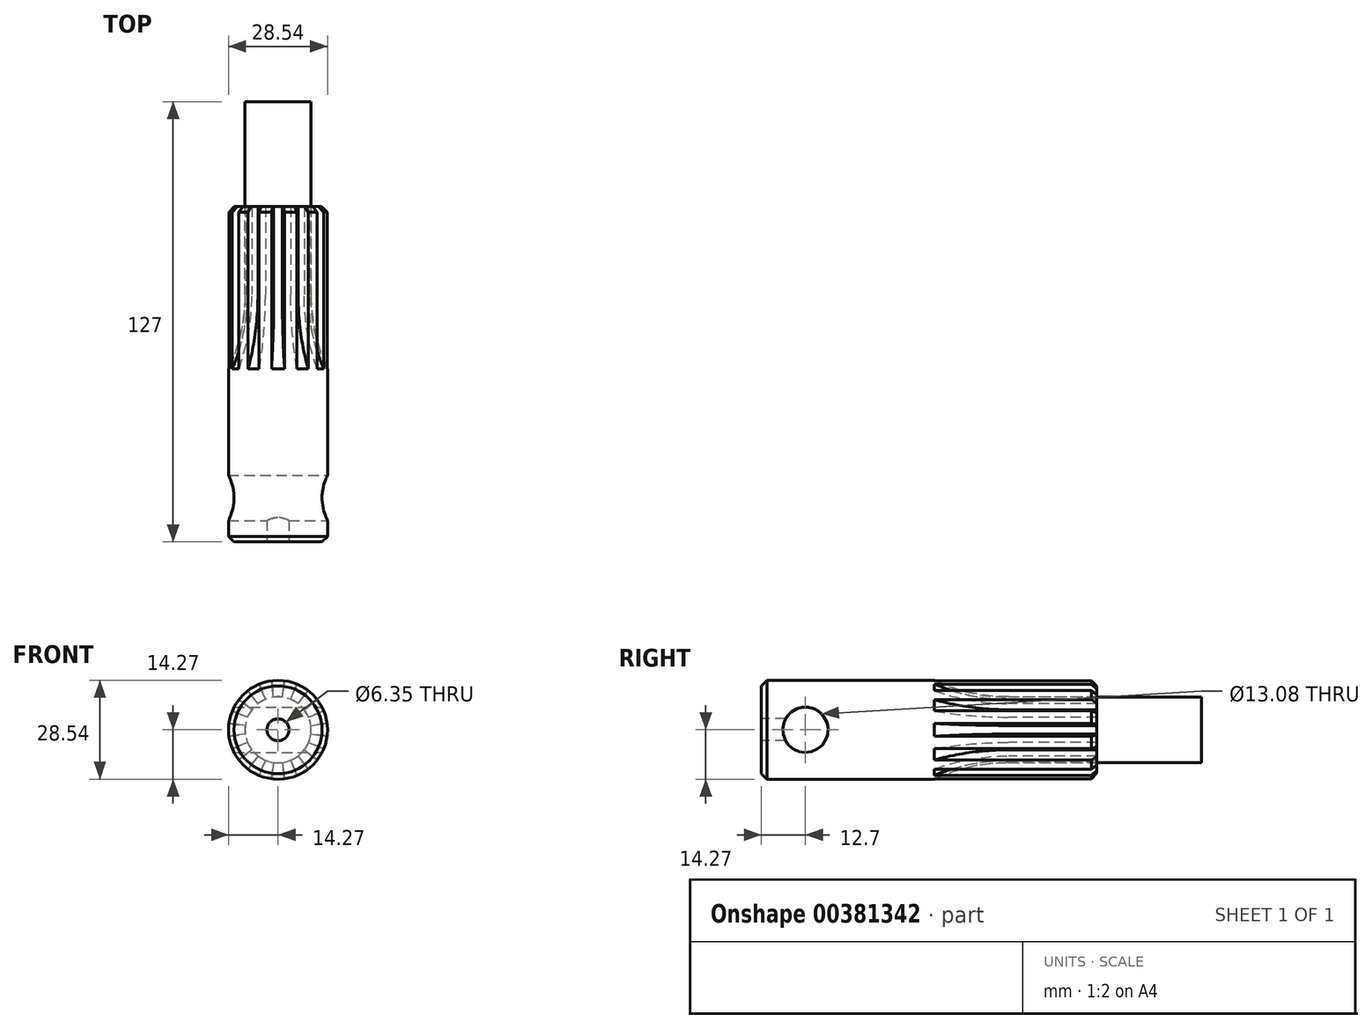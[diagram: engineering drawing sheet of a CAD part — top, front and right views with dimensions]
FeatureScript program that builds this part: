
annotation { "Feature Type Name" : "Feature", "Feature Type Description" : "" }
export const myFeature = defineFeature(function(context is Context, id is Id, definition is map)
    precondition{}
    {
        {
            var Q0;
            Q0=qCreatedBy(makeId("Right.planeOp"),FACE);
            var sketch = newSketch(context, id + "F0", { "sketchPlane" : qUnion([Q0])});
            skLineSegment(sketch, "E0", {"start": v(-154.35, 0) * mm, "end": v(99.65, 0) * mm});
            skSolve(sketch);
        }
        {
            var Q0;
            Q0=qCreatedBy(makeId("Front.planeOp"),FACE);
            var sketch = newSketch(context, id + "F1", { "sketchPlane" : qUnion([Q0])});
            skCircle(sketch, "E1", {"center": v(0, 0) * mm, "radius": 9.51 * mm});
            skSolve(sketch);
        }
        {
            var Q0;
            Q0=qSketchRegion(id+"F1",true);
            extrude(context, id + "F2", {"entities" : qUnion([Q0]), "depth" : 127 * mm});
        }
        {
            var Q0;
            Q0=makeQuery(id+"F2.opExtrude","CAP_FACE",FACE,{"disambiguationData":[OSD([sQuery(id+"F1.wireOp",EDGE,"E1")])],"isStart":false});
            var sketch = newSketch(context, id + "F3", { "sketchPlane" : qUnion([Q0])});
            skCircle(sketch, "E2", {"center": v(0, 0) * mm, "radius": 14.27 * mm});
            skSolve(sketch);
        }
        {
            var Q0;
            Q0=qSketchRegion(id+"F3",true);
            extrude(context, id + "F4", {"entities" : qUnion([Q0]), "operationType" : NewBodyOperationType.ADD, "oppositeDirection" : true, "depth" : 96.77 * mm});
        }
        {
            var Q0;
            Q0=qCreatedBy(makeId("Right.planeOp"),FACE);
            var sketch = newSketch(context, id + "F5", { "sketchPlane" : qUnion([Q0])});
            skCircle(sketch, "E3", {"center": v(-114.3, 0) * mm, "radius": 6.54 * mm});
            skSolve(sketch);
        }
        {
            var Q0;
            Q0=qSketchRegion(id+"F5",true);
            extrude(context, id + "F6", {"entities" : qUnion([Q0]), "operationType" : NewBodyOperationType.REMOVE, "endBound" : BoundingType.SYMMETRIC, "oppositeDirection" : true, "depth" : 50.8 * mm});
        }
        {
            var Q0;
            Q0=makeQuery(id+"F4.boolean.opBoolean","MERGE",FACE,{"derivedFrom":[makeQuery(id+"F2.opExtrude","CAP_FACE",FACE,{"disambiguationData":[OSD([sQuery(id+"F1.wireOp",EDGE,"E1")])],"isStart":false}),makeQuery(id+"F4.opExtrude","CAP_FACE",FACE,{"disambiguationData":[OSD([sQuery(id+"F3.wireOp",EDGE,"E2")])],"isStart":true})]});
            var sketch = newSketch(context, id + "F7", { "sketchPlane" : qUnion([Q0])});
            skCircle(sketch, "E4", {"center": v(0, 0) * mm, "radius": 3.18 * mm});
            skSolve(sketch);
        }
        {
            var Q0;
            Q0=qSketchRegion(id+"F7",true);
            extrude(context, id + "F8", {"entities" : qUnion([Q0]), "operationType" : NewBodyOperationType.REMOVE, "endBound" : BoundingType.UP_TO_NEXT, "oppositeDirection" : true, "depth" : 25.4 * mm});
        }
        {
            var Q0;
            Q0=qCreatedBy(makeId("Right.planeOp"),FACE);
            var sketch = newSketch(context, id + "F9", { "sketchPlane" : qUnion([Q0])});
            skLineSegment(sketch, "E5", {"start": v(-30.23, 9.52) * mm, "end": v(-55.63, 9.52) * mm});
            skArc(sketch, "E6", {"start": v(-89.23, 22.22) * mm, "mid": v(-73.59, 12.8) * mm, "end": v(-55.63, 9.52) * mm});
            skLineSegment(sketch, "E7", {"start": v(-30.23, 9.52) * mm, "end": v(-30.23, 22.22) * mm});
            skLineSegment(sketch, "E8", {"start": v(-30.23, 22.22) * mm, "end": v(-89.23, 22.22) * mm});
            skSolve(sketch);
        }
        {
            var Q0;
            Q0=qSketchRegion(id+"F9",true);
            var Q1;
            Q1=sQuery(id+"F0.wireOp",EDGE,"E0");
            revolve(context, id + "F10", {"operationType" : NewBodyOperationType.REMOVE, "entities" : qUnion([Q0]), "axis" : qUnion([Q1]), "revolveType" : RevolveType.SYMMETRIC, "oppositeDirection" : true, "angle" : 15 * degree});
        }
        {
            var Q0;
            Q0=makeQuery(id+"F10.boolean.opBoolean","COPY",FACE,{"derivedFrom":makeQuery(id+"F10.opRevolve","CAP_FACE",FACE,{"disambiguationData":[OSD([sQuery(id+"F9.wireOp",EDGE,"E5"),sQuery(id+"F9.wireOp",EDGE,"E6"),sQuery(id+"F9.wireOp",EDGE,"E7"),sQuery(id+"F9.wireOp",EDGE,"E8")])],"isStart":true})});
            var Q1;
            Q1=makeQuery(id+"F10.boolean.opBoolean","COPY",FACE,{"derivedFrom":makeQuery(id+"F10.opRevolve","SWEPT_FACE",FACE,{"disambiguationData":[OSD([sQuery(id+"F9.wireOp",EDGE,"E5")])]})});
            var Q2;
            Q2=makeQuery(id+"F10.boolean.opBoolean","COPY",FACE,{"derivedFrom":makeQuery(id+"F10.opRevolve","SWEPT_FACE",FACE,{"disambiguationData":[OSD([sQuery(id+"F9.wireOp",EDGE,"E6")])]})});
            var Q3;
            Q3=makeQuery(id+"F10.boolean.opBoolean","COPY",FACE,{"derivedFrom":makeQuery(id+"F10.opRevolve","CAP_FACE",FACE,{"disambiguationData":[OSD([sQuery(id+"F9.wireOp",EDGE,"E5"),sQuery(id+"F9.wireOp",EDGE,"E6"),sQuery(id+"F9.wireOp",EDGE,"E7"),sQuery(id+"F9.wireOp",EDGE,"E8")])],"isStart":false})});
            var Q4;
            Q4=sQuery(id+"F0.wireOp",EDGE,"E0");
            circularPattern(context, id + "F11", {"faces" : qUnion([Q0, Q1, Q2, Q3]), "axis" : qUnion([Q4]), "angle" : 30 * degree, "instanceCount" : 12, "patternType" : PatternType.FACE});
        }
        {
            var Q0;
            Q0=makeQuery(id+"F11.opPattern","SPLIT",EDGE,{"disambiguationData":[OD(0.0)],"derivedFrom":makeQuery(id+"F4.opExtrude","CAP_EDGE",EDGE,{"disambiguationData":[OSD([sQuery(id+"F3.wireOp",EDGE,"E2")])],"isStart":false})});
            var Q1;
            Q1=makeQuery(id+"F11.opPattern","SPLIT",EDGE,{"disambiguationData":[OD(1.0)],"derivedFrom":makeQuery(id+"F4.opExtrude","CAP_EDGE",EDGE,{"disambiguationData":[OSD([sQuery(id+"F3.wireOp",EDGE,"E2")])],"isStart":false})});
            var Q2;
            Q2=makeQuery(id+"F11.opPattern","SPLIT",EDGE,{"disambiguationData":[OD(2.0)],"derivedFrom":makeQuery(id+"F4.opExtrude","CAP_EDGE",EDGE,{"disambiguationData":[OSD([sQuery(id+"F3.wireOp",EDGE,"E2")])],"isStart":false})});
            var Q3;
            Q3=makeQuery(id+"F11.opPattern","SPLIT",EDGE,{"disambiguationData":[OD(3.0)],"derivedFrom":makeQuery(id+"F4.opExtrude","CAP_EDGE",EDGE,{"disambiguationData":[OSD([sQuery(id+"F3.wireOp",EDGE,"E2")])],"isStart":false})});
            var Q4;
            Q4=makeQuery(id+"F11.opPattern","SPLIT",EDGE,{"disambiguationData":[OD(4.0)],"derivedFrom":makeQuery(id+"F4.opExtrude","CAP_EDGE",EDGE,{"disambiguationData":[OSD([sQuery(id+"F3.wireOp",EDGE,"E2")])],"isStart":false})});
            var Q5;
            Q5=makeQuery(id+"F11.opPattern","SPLIT",EDGE,{"disambiguationData":[OD(5.0)],"derivedFrom":makeQuery(id+"F4.opExtrude","CAP_EDGE",EDGE,{"disambiguationData":[OSD([sQuery(id+"F3.wireOp",EDGE,"E2")])],"isStart":false})});
            var Q6;
            Q6=makeQuery(id+"F11.opPattern","SPLIT",EDGE,{"disambiguationData":[OD(6.0)],"derivedFrom":makeQuery(id+"F4.opExtrude","CAP_EDGE",EDGE,{"disambiguationData":[OSD([sQuery(id+"F3.wireOp",EDGE,"E2")])],"isStart":false})});
            var Q7;
            Q7=makeQuery(id+"F11.opPattern","SPLIT",EDGE,{"disambiguationData":[OD(7.0)],"derivedFrom":makeQuery(id+"F4.opExtrude","CAP_EDGE",EDGE,{"disambiguationData":[OSD([sQuery(id+"F3.wireOp",EDGE,"E2")])],"isStart":false})});
            var Q8;
            Q8=makeQuery(id+"F11.opPattern","SPLIT",EDGE,{"disambiguationData":[OD(8.0)],"derivedFrom":makeQuery(id+"F4.opExtrude","CAP_EDGE",EDGE,{"disambiguationData":[OSD([sQuery(id+"F3.wireOp",EDGE,"E2")])],"isStart":false})});
            var Q9;
            Q9=makeQuery(id+"F11.opPattern","SPLIT",EDGE,{"disambiguationData":[OD(9.0)],"derivedFrom":makeQuery(id+"F4.opExtrude","CAP_EDGE",EDGE,{"disambiguationData":[OSD([sQuery(id+"F3.wireOp",EDGE,"E2")])],"isStart":false})});
            var Q10;
            Q10=makeQuery(id+"F11.opPattern","SPLIT",EDGE,{"disambiguationData":[OD(10.0)],"derivedFrom":makeQuery(id+"F4.opExtrude","CAP_EDGE",EDGE,{"disambiguationData":[OSD([sQuery(id+"F3.wireOp",EDGE,"E2")])],"isStart":false})});
            var Q11;
            Q11=makeQuery(id+"F11.opPattern","SPLIT",EDGE,{"disambiguationData":[OD(11.0)],"derivedFrom":makeQuery(id+"F4.opExtrude","CAP_EDGE",EDGE,{"disambiguationData":[OSD([sQuery(id+"F3.wireOp",EDGE,"E2")])],"isStart":false})});
            chamfer(context, id + "F12", {"entities" : qUnion([Q0, Q1, Q2, Q3, Q4, Q5, Q6, Q7, Q8, Q9, Q10, Q11]), "chamferType" : ChamferType.OFFSET_ANGLE, "width" : 1.6 * mm, "oppositeDirection" : false, "angle" : 45 * degree, "tangentPropagation" : true});
        }
        {
            var Q0;
            Q0=makeQuery(id+"F4.opExtrude","CAP_EDGE",EDGE,{"disambiguationData":[OSD([sQuery(id+"F3.wireOp",EDGE,"E2")])],"isStart":true});
            chamfer(context, id + "F13", {"entities" : qUnion([Q0]), "chamferType" : ChamferType.OFFSET_ANGLE, "width" : 1.59 * mm, "oppositeDirection" : false, "angle" : 45 * degree, "tangentPropagation" : true});
        }
    });
